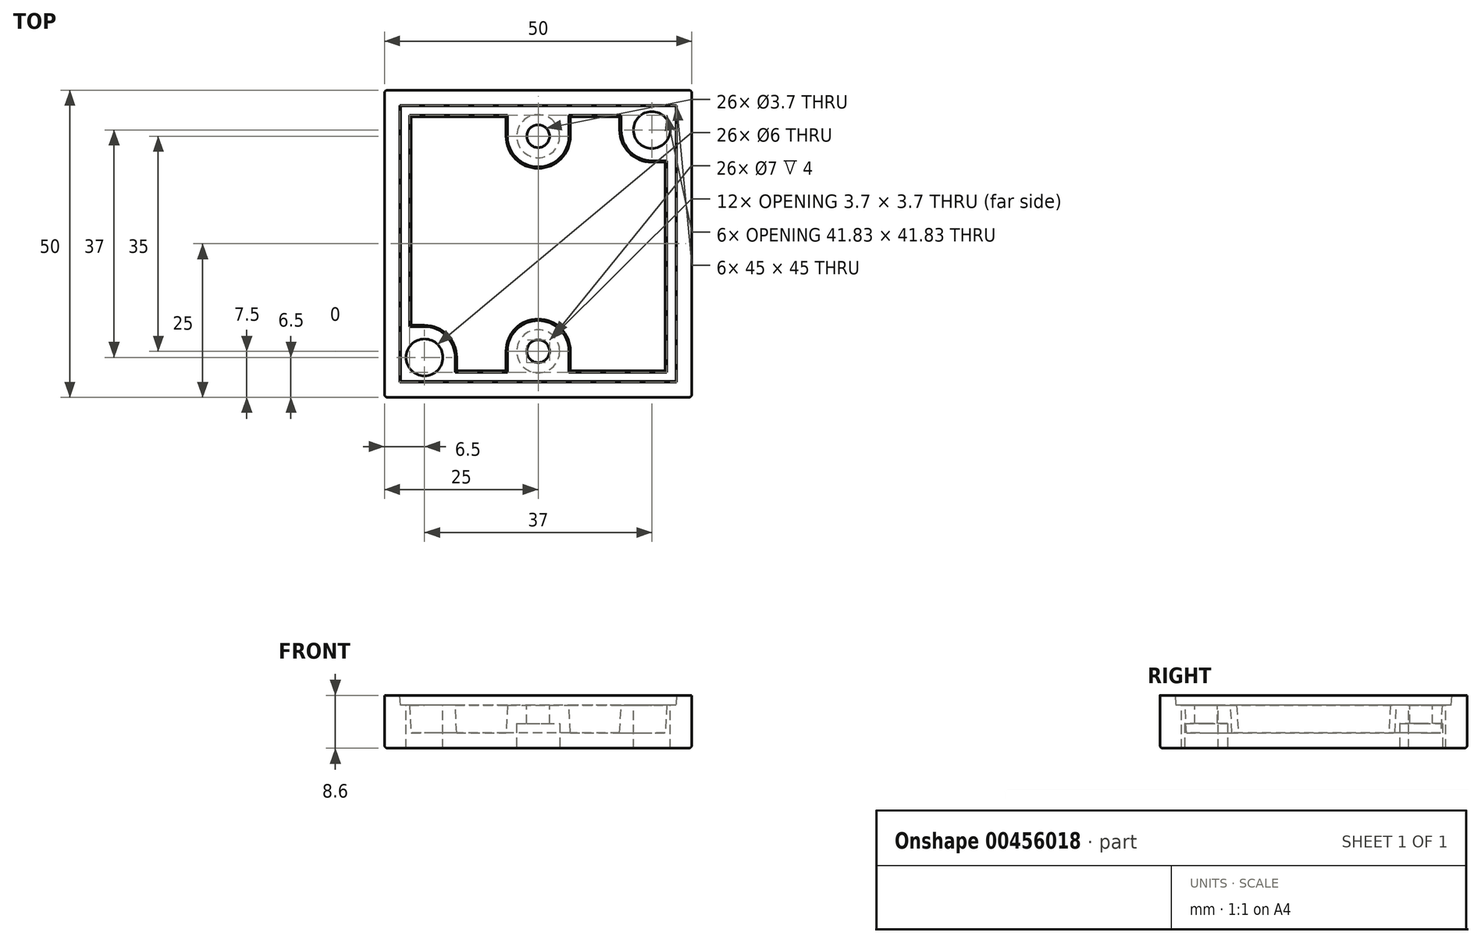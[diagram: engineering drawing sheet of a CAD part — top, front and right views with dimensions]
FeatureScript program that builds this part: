
annotation { "Feature Type Name" : "Feature", "Feature Type Description" : "" }
export const myFeature = defineFeature(function(context is Context, id is Id, definition is map)
    precondition{}
    {
        {
            var Q0;
            Q0=qCreatedBy(makeId("Top.planeOp"),FACE);
            var sketch = newSketch(context, id + "F0", { "sketchPlane" : qUnion([Q0])});
            skLineSegment(sketch, "E0.bottom", {"start": v(25, 25) * mm, "end": v(-25, 25) * mm});
            skLineSegment(sketch, "E0.top", {"start": v(25, -25) * mm, "end": v(-25, -25) * mm});
            skLineSegment(sketch, "E0.left", {"start": v(25, 25) * mm, "end": v(25, -25) * mm});
            skLineSegment(sketch, "E0.right", {"start": v(-25, 25) * mm, "end": v(-25, -25) * mm});
            skPoint(sketch, "E0.middle", {"position": v(0, 0) * mm});
            skSolve(sketch);
        }
        {
            var Q0;
            Q0 = qSketchRegion(id + "F0", true);
            extrude(context, id + "F1", {"entities" : qUnion([Q0]), "oppositeDirection" : true, "depth" : 8.6 * mm});
        }
        {
            var Q0;
            Q0=makeQuery(id+"F1.opExtrude","CAP_FACE",FACE,{"disambiguationData":[OSD([sQuery(id+"F0.wireOp",EDGE,"E0.bottom"),sQuery(id+"F0.wireOp",EDGE,"E0.top"),sQuery(id+"F0.wireOp",EDGE,"E0.left"),sQuery(id+"F0.wireOp",EDGE,"E0.right")])],"isStart":true});
            var sketch = newSketch(context, id + "F2", { "sketchPlane" : qUnion([Q0])});
            skLineSegment(sketch, "E1.0", {"start": v(-22.5, 22.5) * mm, "end": v(-22.5, -22.5) * mm});
            skLineSegment(sketch, "E1.1", {"start": v(22.5, 22.5) * mm, "end": v(-22.5, 22.5) * mm});
            skLineSegment(sketch, "E1.2", {"start": v(22.5, 22.5) * mm, "end": v(22.5, -22.5) * mm});
            skLineSegment(sketch, "E1.3", {"start": v(22.5, -22.5) * mm, "end": v(-22.5, -22.5) * mm});
            skSolve(sketch);
        }
        {
            var Q0;
            Q0 = qSketchRegion(id + "F2", true);
            extrude(context, id + "F3", {"entities" : qUnion([Q0]), "operationType" : NewBodyOperationType.REMOVE, "oppositeDirection" : true, "depth" : 1.6 * mm, "hasDraft" : true, "draftAngle" : 3 * degree, "draftPullDirection" : true});
        }
        {
            var Q0;
            Q0=makeQuery(id+"F3.boolean.opBoolean","COPY",FACE,{"derivedFrom":makeQuery(id+"F3.opExtrude","CAP_FACE",FACE,{"disambiguationData":[OSD([sQuery(id+"F2.wireOp",EDGE,"E1.0"),sQuery(id+"F2.wireOp",EDGE,"E1.1"),sQuery(id+"F2.wireOp",EDGE,"E1.2"),sQuery(id+"F2.wireOp",EDGE,"E1.3")])],"isStart":false})});
            var sketch = newSketch(context, id + "F4", { "sketchPlane" : qUnion([Q0])});
            skLineSegment(sketch, "E2.0", {"start": v(13.5, 20.92) * mm, "end": v(5, 20.92) * mm});
            skLineSegment(sketch, "E2.1", {"start": v(20.92, 13.5) * mm, "end": v(20.92, -20.92) * mm});
            skLineSegment(sketch, "E3", {"start": v(0, 0) * mm, "end": v(20.92, 20.92) * mm, "construction": true});
            skArc(sketch, "E4", {"start": v(13.5, 18.5) * mm, "mid": v(14.96, 14.96) * mm, "end": v(18.5, 13.5) * mm});
            skLineSegment(sketch, "E5", {"start": v(13.5, 18.5) * mm, "end": v(13.5, 20.92) * mm});
            skLineSegment(sketch, "E6", {"start": v(18.5, 13.5) * mm, "end": v(20.92, 13.5) * mm});
            skLineSegment(sketch, "E7", {"start": v(-22.42, 22.42) * mm, "end": v(22.42, -22.42) * mm, "construction": true});
            skLineSegment(sketch, "E8.MirrorCS", {"start": v(-18.5, -13.5) * mm, "end": v(-20.92, -13.5) * mm});
            skLineSegment(sketch, "E9.MirrorCS", {"start": v(-20.92, -13.5) * mm, "end": v(-20.92, 20.92) * mm});
            skLineSegment(sketch, "E10.MirrorCS", {"start": v(-13.5, -20.92) * mm, "end": v(-5, -20.92) * mm});
            skLineSegment(sketch, "E11.MirrorCS", {"start": v(-13.5, -18.5) * mm, "end": v(-13.5, -20.92) * mm});
            skArc(sketch, "E12.MirrorCS", {"start": v(-18.5, -13.5) * mm, "mid": v(-14.96, -14.96) * mm, "end": v(-13.5, -18.5) * mm});
            skArc(sketch, "E13", {"start": v(-5, 17.5) * mm, "mid": v(0, 12.5) * mm, "end": v(5, 17.5) * mm});
            skLineSegment(sketch, "E14", {"start": v(-5, 20.92) * mm, "end": v(-5, 17.5) * mm});
            skLineSegment(sketch, "E15", {"start": v(5, 20.92) * mm, "end": v(5, 17.5) * mm});
            skLineSegment(sketch, "E16.trimOffspring", {"start": v(-5, 20.92) * mm, "end": v(-20.92, 20.92) * mm});
            skArc(sketch, "E17.MirrorCS", {"start": v(-5, -17.5) * mm, "mid": v(0, -12.5) * mm, "end": v(5, -17.5) * mm});
            skLineSegment(sketch, "E18.MirrorCS", {"start": v(5, -20.92) * mm, "end": v(5, -17.5) * mm});
            skLineSegment(sketch, "E19.MirrorCS", {"start": v(-5, -20.92) * mm, "end": v(-5, -17.5) * mm});
            skLineSegment(sketch, "E20.trimOffspring", {"start": v(5, -20.92) * mm, "end": v(20.92, -20.92) * mm});
            skSolve(sketch);
        }
        {
            var Q0;
            Q0 = qSketchRegion(id + "F4", true);
            extrude(context, id + "F5", {"entities" : qUnion([Q0]), "operationType" : NewBodyOperationType.REMOVE, "oppositeDirection" : true, "depth" : 4.5 * mm, "hasDraft" : true, "draftAngle" : 3 * degree, "draftPullDirection" : true});
        }
        {
            var Q0;
            Q0=makeQuery(id+"F3.boolean.opBoolean","COPY",FACE,{"derivedFrom":makeQuery(id+"F3.opExtrude","CAP_FACE",FACE,{"disambiguationData":[OSD([sQuery(id+"F2.wireOp",EDGE,"E1.0"),sQuery(id+"F2.wireOp",EDGE,"E1.1"),sQuery(id+"F2.wireOp",EDGE,"E1.2"),sQuery(id+"F2.wireOp",EDGE,"E1.3")])],"isStart":false})});
            var sketch = newSketch(context, id + "F6", { "sketchPlane" : qUnion([Q0])});
            skCircle(sketch, "E21", {"center": v(0, 17.5) * mm, "radius": 1.85 * mm});
            skCircle(sketch, "E22", {"center": v(18.5, 18.5) * mm, "radius": 3 * mm});
            skCircle(sketch, "E23", {"center": v(0, -17.5) * mm, "radius": 1.85 * mm});
            skCircle(sketch, "E24", {"center": v(-18.5, -18.5) * mm, "radius": 3 * mm});
            skSolve(sketch);
        }
        {
            var Q0;
            Q0 = qSketchRegion(id + "F6", true);
            extrude(context, id + "F7", {"entities" : qUnion([Q0]), "operationType" : NewBodyOperationType.REMOVE, "endBound" : BoundingType.UP_TO_NEXT, "oppositeDirection" : true, "depth" : 25 * mm});
        }
        {
            var Q0;
            Q0=makeQuery(id+"F1.opExtrude","CAP_FACE",FACE,{"disambiguationData":[OSD([sQuery(id+"F0.wireOp",EDGE,"E0.bottom"),sQuery(id+"F0.wireOp",EDGE,"E0.top"),sQuery(id+"F0.wireOp",EDGE,"E0.left"),sQuery(id+"F0.wireOp",EDGE,"E0.right")])],"isStart":false});
            var sketch = newSketch(context, id + "F8", { "sketchPlane" : qUnion([Q0])});
            skCircle(sketch, "E25", {"center": v(0, 17.5) * mm, "radius": 3.5 * mm});
            skCircle(sketch, "E26.MirrorC", {"center": v(0, -17.5) * mm, "radius": 3.5 * mm});
            skSolve(sketch);
        }
        {
            var Q0;
            Q0 = qSketchRegion(id + "F8", true);
            extrude(context, id + "F9", {"entities" : qUnion([Q0]), "operationType" : NewBodyOperationType.REMOVE, "oppositeDirection" : true, "depth" : 4 * mm});
        }
        {
            var Q0;
            Q0=makeQuery(id+"F1.opExtrude","CAP_EDGE",EDGE,{"disambiguationData":[OSD([sQuery(id+"F0.wireOp",EDGE,"E0.top")])],"isStart":false});
            var Q1;
            Q1=makeQuery(id+"F1.opExtrude","SWEPT_EDGE",EDGE,{"disambiguationData":[OSD([sQuery(id+"F0.wireOp",EDGE,"E0.top"),sQuery(id+"F0.wireOp",EDGE,"E0.right")])]});
            var Q2;
            Q2=makeQuery(id+"F1.opExtrude","CAP_EDGE",EDGE,{"disambiguationData":[OSD([sQuery(id+"F0.wireOp",EDGE,"E0.right")])],"isStart":false});
            var Q3;
            Q3=makeQuery(id+"F7.boolean.opBoolean","COPY",EDGE,{"derivedFrom":makeQuery(id+"F7.opExtrude","TWEAK_EDGE",EDGE,{"derivedFrom":[makeQuery(id+"F1.opExtrude","CAP_FACE",FACE,{"disambiguationData":[OSD([sQuery(id+"F0.wireOp",EDGE,"E0.bottom"),sQuery(id+"F0.wireOp",EDGE,"E0.top"),sQuery(id+"F0.wireOp",EDGE,"E0.left"),sQuery(id+"F0.wireOp",EDGE,"E0.right")])],"isStart":false}),makeQuery(id+"F6.imprint","IMPRINT",EDGE,{"derivedFrom":sQuery(id+"F6.wireOp",EDGE,"E24")})]})});
            var Q4;
            Q4=makeQuery(id+"F7.boolean.opBoolean","COPY",EDGE,{"derivedFrom":makeQuery(id+"F7.opExtrude","TWEAK_EDGE",EDGE,{"derivedFrom":[makeQuery(id+"F1.opExtrude","CAP_FACE",FACE,{"disambiguationData":[OSD([sQuery(id+"F0.wireOp",EDGE,"E0.bottom"),sQuery(id+"F0.wireOp",EDGE,"E0.top"),sQuery(id+"F0.wireOp",EDGE,"E0.left"),sQuery(id+"F0.wireOp",EDGE,"E0.right")])],"isStart":false}),makeQuery(id+"F6.imprint","IMPRINT",EDGE,{"derivedFrom":sQuery(id+"F6.wireOp",EDGE,"E22")})]})});
            var Q5;
            Q5=makeQuery(id+"F1.opExtrude","SWEPT_EDGE",EDGE,{"disambiguationData":[OSD([sQuery(id+"F0.wireOp",EDGE,"E0.bottom"),sQuery(id+"F0.wireOp",EDGE,"E0.right")])]});
            var Q6;
            Q6=makeQuery(id+"F1.opExtrude","CAP_EDGE",EDGE,{"disambiguationData":[OSD([sQuery(id+"F0.wireOp",EDGE,"E0.bottom")])],"isStart":false});
            var Q7;
            Q7=makeQuery(id+"F1.opExtrude","SWEPT_EDGE",EDGE,{"disambiguationData":[OSD([sQuery(id+"F0.wireOp",EDGE,"E0.bottom"),sQuery(id+"F0.wireOp",EDGE,"E0.left")])]});
            var Q8;
            Q8=makeQuery(id+"F1.opExtrude","CAP_EDGE",EDGE,{"disambiguationData":[OSD([sQuery(id+"F0.wireOp",EDGE,"E0.left")])],"isStart":false});
            var Q9;
            Q9=makeQuery(id+"F1.opExtrude","SWEPT_EDGE",EDGE,{"disambiguationData":[OSD([sQuery(id+"F0.wireOp",EDGE,"E0.top"),sQuery(id+"F0.wireOp",EDGE,"E0.left")])]});
            fillet(context, id + "F10", {"entities" : qUnion([Q0, Q1, Q2, Q3, Q4, Q5, Q6, Q7, Q8, Q9]), "radius" : 0.5 * mm, "tangentPropagation" : true, "allowEdgeOverflow" : false});
        }
    });
